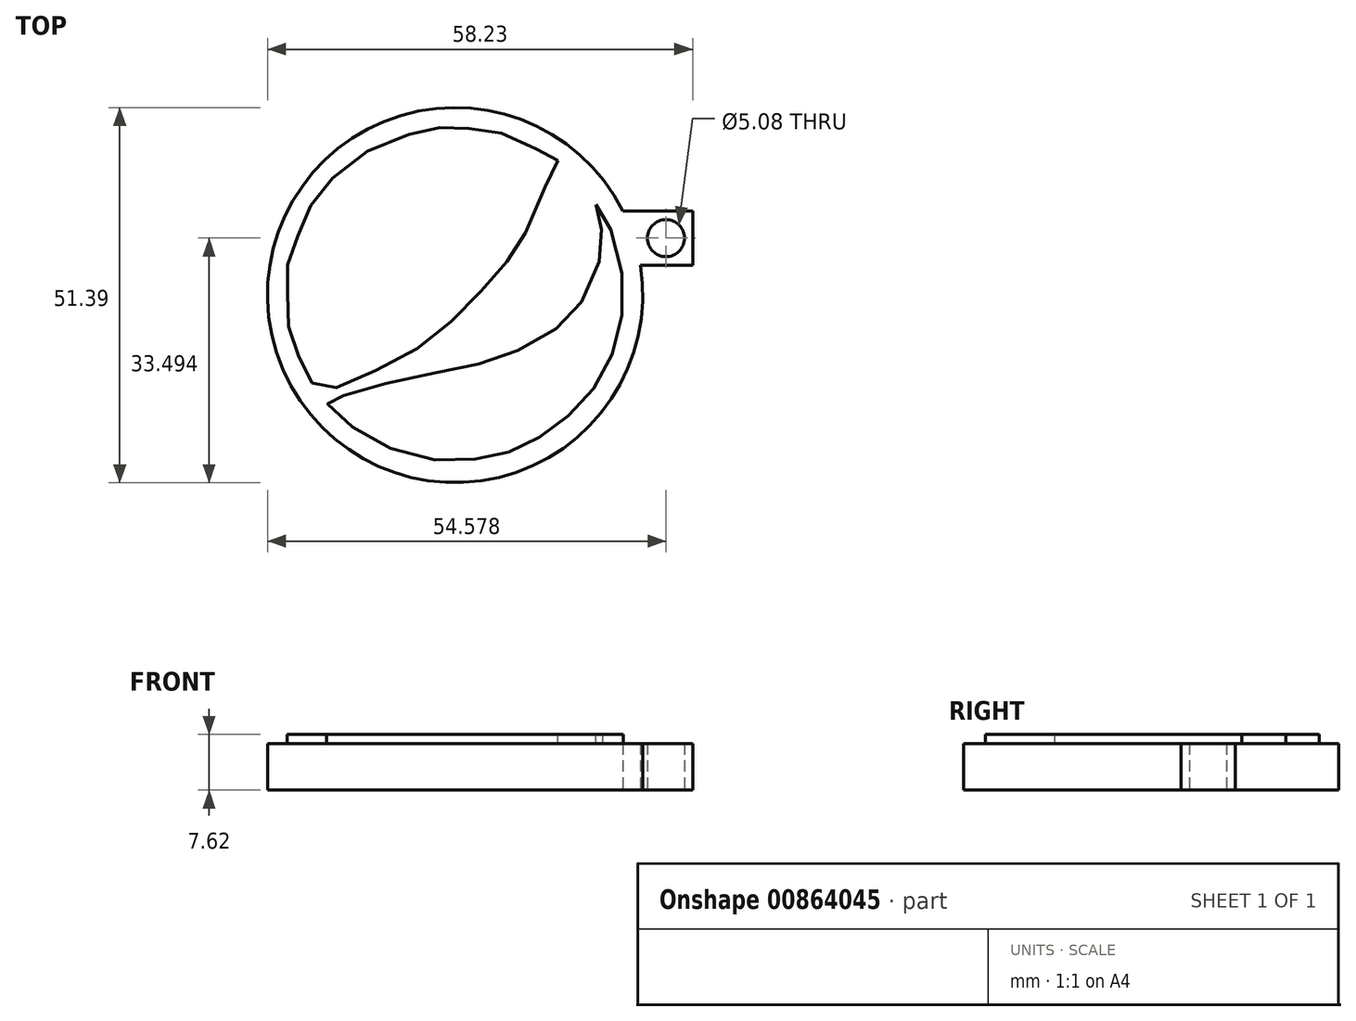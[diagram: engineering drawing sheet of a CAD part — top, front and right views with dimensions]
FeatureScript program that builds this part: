
annotation { "Feature Type Name" : "Feature", "Feature Type Description" : "" }
export const myFeature = defineFeature(function(context is Context, id is Id, definition is map)
    precondition{}
    {
        {
            var Q0;
            Q0=qCreatedBy(makeId("Top.planeOp"),FACE);
            var sketch = newSketch(context, id + "F0", { "sketchPlane" : qUnion([Q0])});
            skFitSpline(sketch, "E0", {"points": [v(11.4, 17.7) * mm, v(10.68, 16.37) * mm, v(7.19, 8.2) * mm, v(4.7, 4.21) * mm, v(0.82, -0.32) * mm, v(-4.36, -5.39) * mm, v(-10.61, -9.7) * mm, v(-18.06, -13.05) * mm, v(-21.3, -13.8) * mm, v(-23.23, -10.78) * mm, v(-24.53, -8.3) * mm, v(-25.6, -3.99) * mm, v(-25.6, 0) * mm, v(-25.6, 3.24) * mm, v(-24.53, 6.48) * mm, v(-22.9, 10.58) * mm, v(-20.54, 14.14) * mm, v(-15.14, 18.67) * mm, v(-8.24, 21.47) * mm, v(-4.68, 22.23) * mm, v(-1.34, 22.12) * mm, v(2.55, 21.69) * mm, v(7.5, 19.85) * mm, v(11.07, 17.7) * mm, v(11.4, 17.7) * mm]});
            skFitSpline(sketch, "E1", {"points": [v(16.64, 11.65) * mm, v(17.15, 9.22) * mm, v(17.54, 6.15) * mm, v(15.17, -0.86) * mm, v(11.4, -5.17) * mm, v(4.49, -8.95) * mm, v(-1.98, -10.78) * mm, v(-11.58, -12.72) * mm, v(-18.76, -14.7) * mm, v(-20.25, -15.2) * mm, v(-18.6, -17.25) * mm, v(-12.88, -21.14) * mm, v(-4.68, -23.4) * mm, v(1.47, -22.97) * mm, v(5.78, -21.9) * mm, v(10.1, -19.41) * mm, v(14.23, -15.96) * mm, v(17.77, -11.16) * mm, v(19.89, -5.17) * mm, v(20.23, 1.87) * mm, v(18.05, 9.59) * mm, v(16.64, 11.65) * mm]});
            skCircle(sketch, "E2", {"center": v(-2.7, -0.63) * mm, "radius": 24.9 * mm});
            skCircle(sketch, "E3", {"center": v(-2.7, -0.63) * mm, "radius": 23.74 * mm});
            skSolve(sketch);
        }
        {
            var Q0;
            Q0=qCreatedBy(makeId("Top.planeOp"),FACE);
            var sketch = newSketch(context, id + "F1", { "sketchPlane" : qUnion([Q0])});
            skCircle(sketch, "E4", {"center": v(-2.67, -0.74) * mm, "radius": 25.7 * mm});
            skLineSegment(sketch, "E5", {"start": v(20.3, 10.76) * mm, "end": v(29.87, 10.76) * mm});
            skLineSegment(sketch, "E6", {"start": v(29.87, 10.76) * mm, "end": v(29.87, 3.35) * mm});
            skLineSegment(sketch, "E7", {"start": v(29.87, 3.35) * mm, "end": v(22.7, 3.35) * mm});
            skPoint(sketch, "E8", {"position": v(26.22, 7.05) * mm});
            skSolve(sketch);
        }
        {
            var Q0;
            Q0=makeQuery(id+"F0.imprint","IMPRINT",FACE,{"disambiguationData":[TD([[makeQuery(id+"F0.imprint","IMPRINT",EDGE,{"derivedFrom":sQuery(id+"F0.wireOp",EDGE,"E0")}),-1.0]])]});
            var Q1;
            Q1=makeQuery(id+"F0.imprint","IMPRINT",FACE,{"disambiguationData":[TD([[makeQuery(id+"F0.imprint","IMPRINT",EDGE,{"derivedFrom":sQuery(id+"F0.wireOp",EDGE,"E1")}),1.0]])]});
            extrude(context, id + "F2", {"entities" : qUnion([Q0, Q1]), "depth" : 7.62 * mm, "offsetDistance" : 25.4 * mm});
        }
        {
            var Q0;
            Q0=makeQuery(id+"F1.imprint","IMPRINT",FACE,{"disambiguationData":[TD([[makeQuery(id+"F1.imprint","IMPRINT",EDGE,{"derivedFrom":sQuery(id+"F1.wireOp",EDGE,"E4")}),1.0]])]});
            var Q1;
            {var subQ0=sQuery(id+"F1.wireOp",EDGE,"E5");Q1=makeQuery(id+"F1.imprint","IMPRINT",FACE,{"disambiguationData":[TD([[makeQuery(id+"F1.imprint","IMPRINT",EDGE,{"derivedFrom":subQ0}),-1.0]])]});}
            extrude(context, id + "F3", {"entities" : qUnion([Q0, Q1]), "operationType" : NewBodyOperationType.ADD, "depth" : 6.35 * mm, "offsetDistance" : 25.4 * mm});
        }
        {
            var Q0;
            Q0=sQuery(id+"F1.wireOp",VERTEX,"E8");
            var Q1;
            Q1=makeQuery(id+"F2.opExtrude","SWEPT_BODY",BODY,{"disambiguationData":[OSD([sQuery(id+"F0.wireOp",EDGE,"E0")])]});
            hole(context, id + "F4", {"style" : HoleStyle.SIMPLE, "endStyle" : HoleEndStyle.THROUGH, "oppositeDirection" : true, "holeDiameter" : 5.08 * mm, "majorDiameter" : 6.35 * mm, "isTappedThrough" : true, "tappedDepth" : 12.7 * mm, "tapClearance" : 3, "locations" : qUnion([Q0]), "scope" : qUnion([Q1])});
        }
    });
